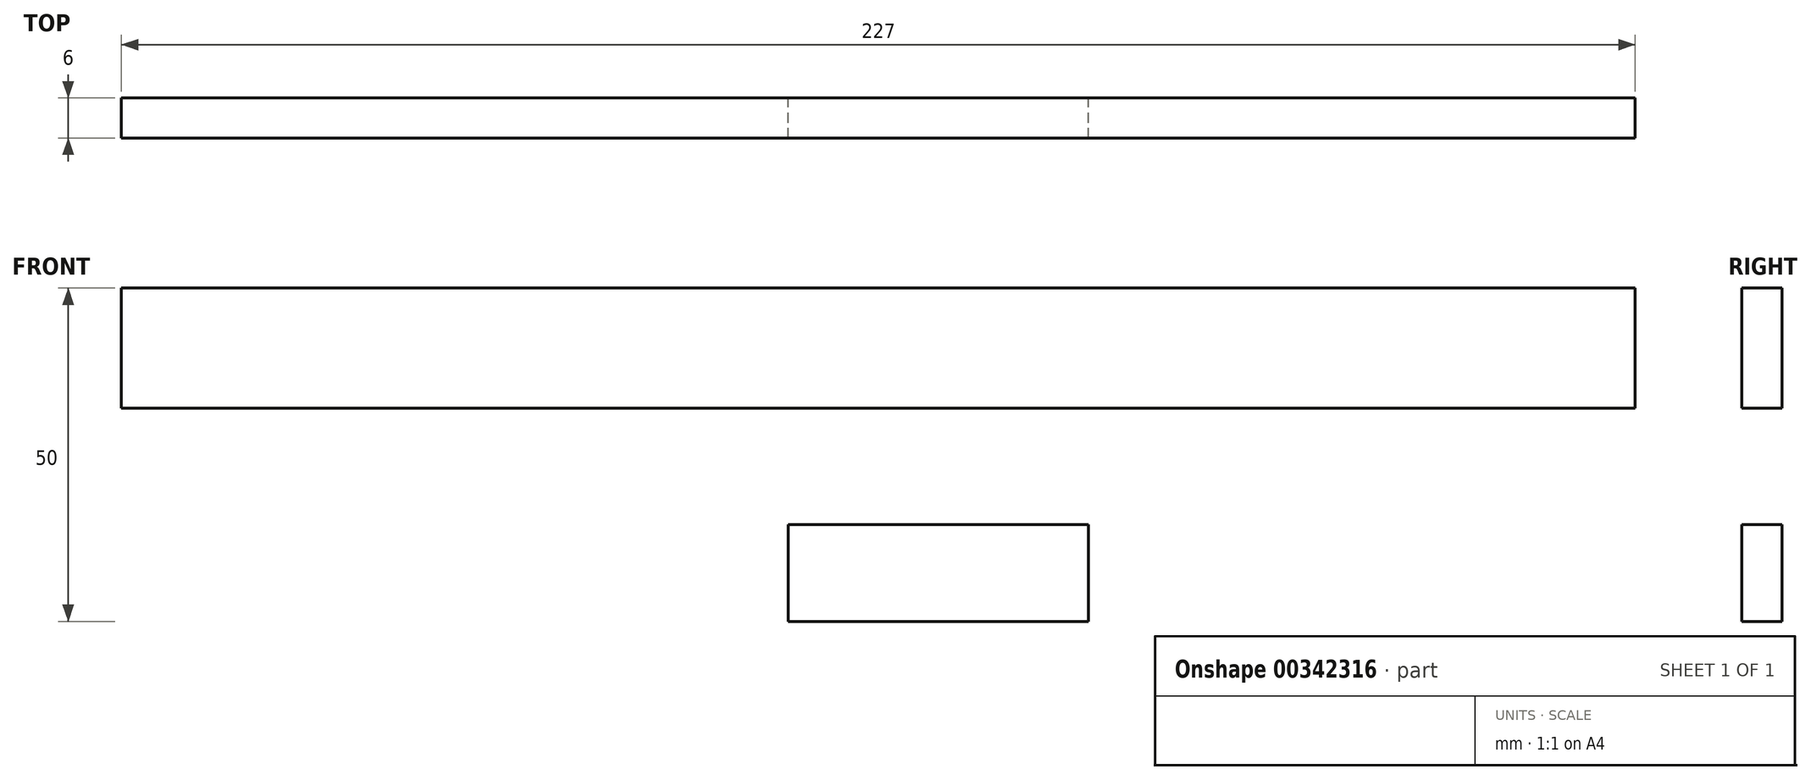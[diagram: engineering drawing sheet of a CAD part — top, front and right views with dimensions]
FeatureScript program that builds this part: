
annotation { "Feature Type Name" : "Feature", "Feature Type Description" : "" }
export const myFeature = defineFeature(function(context is Context, id is Id, definition is map)
    precondition{}
    {
        {
            var Q0;
            Q0=qCreatedBy(makeId("Front.planeOp"),FACE);
            var sketch = newSketch(context, id + "F0", { "sketchPlane" : qUnion([Q0])});
            skLineSegment(sketch, "E0.bottom", {"start": v(0, 0) * mm, "end": v(45, 0) * mm});
            skLineSegment(sketch, "E0.top", {"start": v(0, 14.5) * mm, "end": v(45, 14.5) * mm});
            skLineSegment(sketch, "E0.left", {"start": v(0, 0) * mm, "end": v(0, 14.5) * mm});
            skLineSegment(sketch, "E0.right", {"start": v(45, 0) * mm, "end": v(45, 14.5) * mm});
            skLineSegment(sketch, "E1.bottom", {"start": v(-100, 32) * mm, "end": v(127, 32) * mm});
            skLineSegment(sketch, "E1.top", {"start": v(-100, 50) * mm, "end": v(127, 50) * mm});
            skLineSegment(sketch, "E1.left", {"start": v(-100, 32) * mm, "end": v(-100, 50) * mm});
            skLineSegment(sketch, "E1.right", {"start": v(127, 32) * mm, "end": v(127, 50) * mm});
            skSolve(sketch);
        }
        {
            var Q0;
            Q0 = qSketchRegion(id + "F0", true);
            extrude(context, id + "F1", {"entities" : qUnion([Q0]), "depth" : 6 * mm, "offsetDistance" : 25 * mm});
        }
    });
